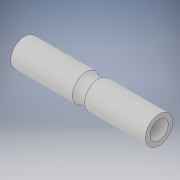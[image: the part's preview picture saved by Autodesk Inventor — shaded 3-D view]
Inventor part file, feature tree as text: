
AUTODESK INVENTOR PART (.ipt)
format: ipt  version: 2018.3 (Build 223284000, 284)  size: 124,416 bytes
history: native  units: in
note: dims shown in document units (in); Inventor stores cm internally (conversion verified against a paired STEP export)
features: revolve x1, sketch x1
ambient origin geometry x8: Origin, YZ Plane, XZ Plane, XY Plane, X Axis, Y Axis, Z Axis, Center Point
bodies: Solid1 (feature_tree)
feature tree (2):
  revolve  "Revolution1"  [1 undecoded]
  sketch  "Sketch1"  dims[d0=0.785in d1=0.078in d2=0.32in d3=0.38in d4=0.12in d5=0.067in d6=0.12in d7=0.03in d8=90.0deg]
note: 1 required parameter value undecoded (feature->parameter linkage not recoverable at this tier; creation-order binding heuristic only, values carry confidence <= 0.55)
